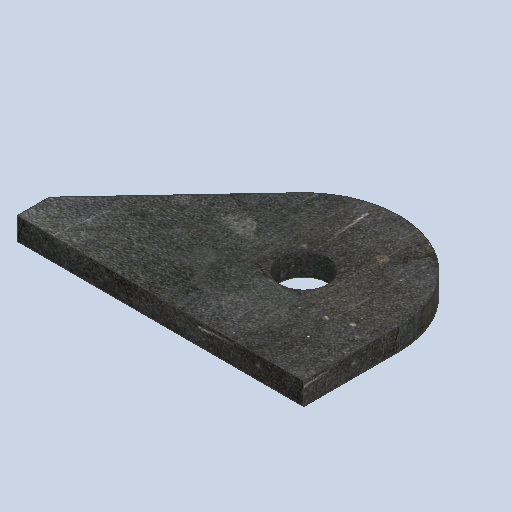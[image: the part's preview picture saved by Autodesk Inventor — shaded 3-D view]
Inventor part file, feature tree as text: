
AUTODESK INVENTOR PART (.ipt)
format: ipt  version: 2023 (Build 270158000, 158)  size: 1,927,168 bytes
history: native  units: mm
features: other x3, sketch x1
ambient origin geometry x8: Origin, YZ Plane, XZ Plane, XY Plane, X Axis, Y Axis, Z Axis, Center Point
bodies: Body1 (feature_tree)
feature tree (4):
  other  "Cara2"
  sketch  "Boceto2"  dims[d7=60.0mm d8=20.0mm d9=60.0mm d10=180.0mm d11=30.0mm d12=14.0mm]
  other  "Placa2"
  other  "Definición1"
